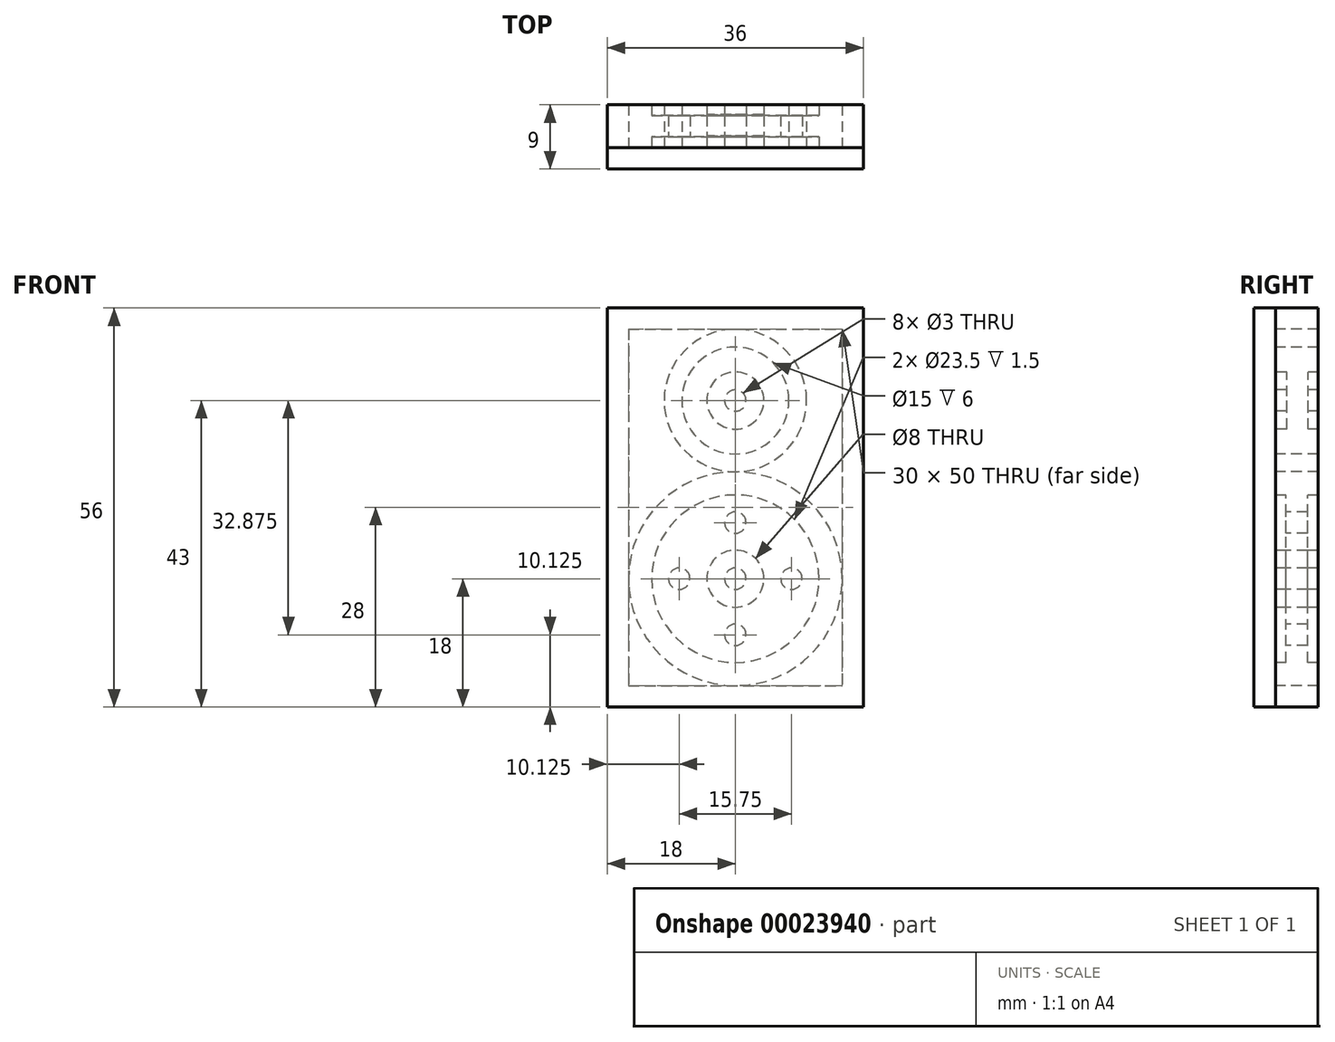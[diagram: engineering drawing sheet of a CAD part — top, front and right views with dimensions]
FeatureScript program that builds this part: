
annotation { "Feature Type Name" : "Feature", "Feature Type Description" : "" }
export const myFeature = defineFeature(function(context is Context, id is Id, definition is map)
    precondition{}
    {
        {
            var Q0;
            Q0=qCreatedBy(makeId("Right.planeOp"),FACE);
            var sketch = newSketch(context, id + "F0", { "sketchPlane" : qUnion([Q0])});
            skLineSegment(sketch, "E0.rect.bottom", {"start": v(-3, 1.5) * mm, "end": v(3, 1.5) * mm});
            skLineSegment(sketch, "E0.rect.top", {"start": v(-3, 4) * mm, "end": v(3, 4) * mm});
            skLineSegment(sketch, "E0.rect.left", {"start": v(-3, 4) * mm, "end": v(-3, 1.5) * mm});
            skLineSegment(sketch, "E0.rect.right", {"start": v(3, 4) * mm, "end": v(3, 1.5) * mm});
            skPoint(sketch, "E0.rect.middle", {"position": v(0, 2.75) * mm});
            skLineSegment(sketch, "E1.rect.bottom", {"start": v(1.5, 1.5) * mm, "end": v(-1.5, 1.5) * mm});
            skLineSegment(sketch, "E1.rect.top", {"start": v(1.5, 11.75) * mm, "end": v(-1.5, 11.75) * mm});
            skLineSegment(sketch, "E1.rect.left", {"start": v(1.5, 1.5) * mm, "end": v(1.5, 11.75) * mm});
            skLineSegment(sketch, "E1.rect.right", {"start": v(-1.5, 1.5) * mm, "end": v(-1.5, 11.75) * mm});
            skPoint(sketch, "E1.rect.middle", {"position": v(0, 6.62) * mm});
            skLineSegment(sketch, "E2.rect.bottom", {"start": v(-3, 15) * mm, "end": v(3, 15) * mm});
            skLineSegment(sketch, "E2.rect.left", {"start": v(-3, 15) * mm, "end": v(-3, 11.75) * mm});
            skLineSegment(sketch, "E2.rect.top", {"start": v(-3, 11.75) * mm, "end": v(3, 11.75) * mm});
            skLineSegment(sketch, "E2.rect.right", {"start": v(3, 15) * mm, "end": v(3, 11.75) * mm});
            skLineSegment(sketch, "E3", {"start": v(-14.88, 0) * mm, "end": v(15.69, 0) * mm, "construction": true});
            skLineSegment(sketch, "E4", {"start": v(1.5, 1.5) * mm, "end": v(3, 1.5) * mm});
            skLineSegment(sketch, "E5", {"start": v(-3, 1.5) * mm, "end": v(-1.5, 1.5) * mm});
            skLineSegment(sketch, "E6", {"start": v(-3, 4) * mm, "end": v(-3, 11.75) * mm, "construction": true});
            skLineSegment(sketch, "E7", {"start": v(3, 4) * mm, "end": v(3, 11.75) * mm, "construction": true});
            skPoint(sketch, "E8.rect.middle", {"position": v(0.12, 29.5) * mm});
            skLineSegment(sketch, "E9", {"start": v(-3, 29) * mm, "end": v(-3, 32.5) * mm, "construction": true});
            skLineSegment(sketch, "E10.rect.bottom", {"start": v(-3, 26.5) * mm, "end": v(3, 26.5) * mm});
            skLineSegment(sketch, "E10.rect.top", {"start": v(-3, 29) * mm, "end": v(3, 29) * mm});
            skLineSegment(sketch, "E10.rect.left", {"start": v(-3, 29) * mm, "end": v(-3, 26.5) * mm});
            skLineSegment(sketch, "E10.rect.right", {"start": v(3, 29) * mm, "end": v(3, 26.5) * mm});
            skPoint(sketch, "E10.rect.middle", {"position": v(0, 27.75) * mm});
            skLineSegment(sketch, "E8.rect.bottom", {"start": v(1.62, 26.5) * mm, "end": v(-1.38, 26.5) * mm});
            skLineSegment(sketch, "E8.rect.left", {"start": v(1.62, 26.5) * mm, "end": v(1.62, 32.5) * mm});
            skLineSegment(sketch, "E8.rect.right", {"start": v(-1.38, 26.5) * mm, "end": v(-1.38, 32.5) * mm});
            skLineSegment(sketch, "E11.rect.bottom", {"start": v(-3, 35) * mm, "end": v(3, 35) * mm});
            skLineSegment(sketch, "E11.rect.left", {"start": v(-3, 35) * mm, "end": v(-3, 32.5) * mm});
            skLineSegment(sketch, "E11.rect.top", {"start": v(-3, 32.5) * mm, "end": v(3, 32.5) * mm});
            skLineSegment(sketch, "E11.rect.right", {"start": v(3, 35) * mm, "end": v(3, 32.5) * mm});
            skLineSegment(sketch, "E12", {"start": v(3, 29) * mm, "end": v(3, 32.5) * mm, "construction": true});
            skLineSegment(sketch, "E13", {"start": v(1.62, 26.5) * mm, "end": v(3, 26.5) * mm});
            skLineSegment(sketch, "E14", {"start": v(-3, 26.5) * mm, "end": v(-1.38, 26.5) * mm});
            skLineSegment(sketch, "E8.rect.top", {"start": v(1.62, 32.5) * mm, "end": v(-1.38, 32.5) * mm});
            skLineSegment(sketch, "E15", {"start": v(-18.67, 25) * mm, "end": v(16.68, 25) * mm, "construction": true});
            skLineSegment(sketch, "E16", {"start": v(-3, 1.5) * mm, "end": v(-3, 38.38) * mm, "construction": true});
            skLineSegment(sketch, "E17", {"start": v(3, 1.5) * mm, "end": v(3, 82.02) * mm, "construction": true});
            skSolve(sketch);
        }
        {
            var Q0;
            Q0=makeQuery(id+"F0.imprint","IMPRINT",FACE,{"disambiguationData":[TD([[makeQuery(id+"F0.imprint","IMPRINT",EDGE,{"derivedFrom":sQuery(id+"F0.wireOp",EDGE,"E2.rect.bottom")}),-1.0]])]});
            var Q1;
            {var subQ1=sQuery(id+"F0.wireOp",EDGE,"E1.rect.right");var subQ5=sQuery(id+"F0.wireOp",EDGE,"E0.rect.top");var subQ6=makeQuery(id+"F0.imprint","INTERSECT",VERTEX,{"derivedFrom":[subQ5,subQ1]});Q1=makeQuery(id+"F0.imprint","IMPRINT",FACE,{"disambiguationData":[TD([[makeQuery(id+"F0.imprint","IMPRINT",EDGE,{"disambiguationData":[TD([[subQ6,-1.0]])],"derivedFrom":subQ5}),1.0]])]});}
            var Q2;
            {var subQ4=sQuery(id+"F0.wireOp",EDGE,"E1.rect.bottom");Q2=makeQuery(id+"F0.imprint","IMPRINT",FACE,{"disambiguationData":[TD([[makeQuery(id+"F0.imprint","IMPRINT",EDGE,{"derivedFrom":subQ4}),-1.0]])]});}
            var Q3;
            {var subQ5=sQuery(id+"F0.wireOp",EDGE,"E0.rect.left");Q3=makeQuery(id+"F0.imprint","IMPRINT",FACE,{"disambiguationData":[TD([[makeQuery(id+"F0.imprint","IMPRINT",EDGE,{"derivedFrom":subQ5}),1.0]])]});}
            var Q4;
            {var subQ5=sQuery(id+"F0.wireOp",EDGE,"E0.rect.right");Q4=makeQuery(id+"F0.imprint","IMPRINT",FACE,{"disambiguationData":[TD([[makeQuery(id+"F0.imprint","IMPRINT",EDGE,{"derivedFrom":subQ5}),-1.0]])]});}
            var Q5;
            Q5=sQuery(id+"F0.wireOp",EDGE,"E3");
            revolve(context, id + "F1", {"entities" : qUnion([Q0, Q1, Q2, Q3, Q4]), "axis" : qUnion([Q5]), "revolveType" : RevolveType.FULL});
        }
        {
            var Q0;
            Q0=makeQuery(id+"F1.opRevolve","SWEPT_FACE",FACE,{"disambiguationData":[OSD([sQuery(id+"F0.wireOp",EDGE,"E1.rect.right")])]});
            var sketch = newSketch(context, id + "F2", { "sketchPlane" : qUnion([Q0])});
            skCircle(sketch, "E18", {"center": v(0, 7.88) * mm, "radius": 1.5 * mm});
            skLineSegment(sketch, "E19", {"start": v(0, 4) * mm, "end": v(0, 6.38) * mm, "construction": true});
            skLineSegment(sketch, "E20", {"start": v(0, 9.38) * mm, "end": v(0, 11.75) * mm, "construction": true});
            skCircle(sketch, "E21.1.0", {"center": v(-7.88, 0) * mm, "radius": 1.5 * mm});
            skCircle(sketch, "E21.2.0", {"center": v(0, -7.88) * mm, "radius": 1.5 * mm});
            skCircle(sketch, "E21.3.0", {"center": v(7.88, 0) * mm, "radius": 1.5 * mm});
            skPoint(sketch, "E21.center", {"position": v(0, 0) * mm});
            skSolve(sketch);
        }
        {
            var Q0;
            Q0=makeQuery(id+"F2.imprint","IMPRINT",FACE,{"disambiguationData":[TD([[makeQuery(id+"F2.imprint","IMPRINT",EDGE,{"derivedFrom":sQuery(id+"F2.wireOp",EDGE,"E18")}),1.0]])]});
            var Q1;
            Q1=makeQuery(id+"F2.imprint","IMPRINT",FACE,{"disambiguationData":[TD([[makeQuery(id+"F2.imprint","IMPRINT",EDGE,{"derivedFrom":sQuery(id+"F2.wireOp",EDGE,"E21.3.0")}),1.0]])]});
            var Q2;
            Q2=makeQuery(id+"F2.imprint","IMPRINT",FACE,{"disambiguationData":[TD([[makeQuery(id+"F2.imprint","IMPRINT",EDGE,{"derivedFrom":sQuery(id+"F2.wireOp",EDGE,"E21.1.0")}),1.0]])]});
            var Q3;
            Q3=makeQuery(id+"F2.imprint","IMPRINT",FACE,{"disambiguationData":[TD([[makeQuery(id+"F2.imprint","IMPRINT",EDGE,{"derivedFrom":sQuery(id+"F2.wireOp",EDGE,"E21.2.0")}),1.0]])]});
            extrude(context, id + "F3", {"entities" : qUnion([Q0, Q1, Q2, Q3]), "operationType" : NewBodyOperationType.REMOVE, "oppositeDirection" : true, "depth" : 3 * mm});
        }
        {
            var Q0;
            {var subQ3=sQuery(id+"F0.wireOp",EDGE,"E8.rect.bottom");Q0=makeQuery(id+"F0.imprint","IMPRINT",FACE,{"disambiguationData":[TD([[makeQuery(id+"F0.imprint","IMPRINT",EDGE,{"derivedFrom":subQ3}),-1.0]])]});}
            var Q1;
            {var subQ0=sQuery(id+"F0.wireOp",EDGE,"E8.rect.top");Q1=makeQuery(id+"F0.imprint","IMPRINT",FACE,{"disambiguationData":[TD([[makeQuery(id+"F0.imprint","IMPRINT",EDGE,{"derivedFrom":subQ0}),1.0]])]});}
            var Q2;
            Q2=makeQuery(id+"F0.imprint","IMPRINT",FACE,{"disambiguationData":[TD([[makeQuery(id+"F0.imprint","IMPRINT",EDGE,{"derivedFrom":sQuery(id+"F0.wireOp",EDGE,"E11.rect.bottom")}),-1.0]])]});
            var Q3;
            {var subQ4=sQuery(id+"F0.wireOp",EDGE,"E10.rect.right");Q3=makeQuery(id+"F0.imprint","IMPRINT",FACE,{"disambiguationData":[TD([[makeQuery(id+"F0.imprint","IMPRINT",EDGE,{"derivedFrom":subQ4}),-1.0]])]});}
            var Q4;
            {var subQ4=sQuery(id+"F0.wireOp",EDGE,"E10.rect.left");Q4=makeQuery(id+"F0.imprint","IMPRINT",FACE,{"disambiguationData":[TD([[makeQuery(id+"F0.imprint","IMPRINT",EDGE,{"derivedFrom":subQ4}),1.0]])]});}
            var Q5;
            Q5=sQuery(id+"F0.wireOp",EDGE,"E15");
            revolve(context, id + "F4", {"entities" : qUnion([Q0, Q1, Q2, Q3, Q4]), "axis" : qUnion([Q5]), "revolveType" : RevolveType.FULL});
        }
        {
            var Q0;
            Q0=makeQuery(id+"F4.opRevolve","SWEPT_FACE",FACE,{"disambiguationData":[OSD([sQuery(id+"F0.wireOp",EDGE,"E8.rect.right")])]});
            var sketch = newSketch(context, id + "F5", { "sketchPlane" : qUnion([Q0])});
            skCircle(sketch, "E22", {"center": v(0, 30.75) * mm, "radius": 1.5 * mm});
            skLineSegment(sketch, "E23", {"start": v(0, 32.25) * mm, "end": v(0, 32.5) * mm});
            skLineSegment(sketch, "E24", {"start": v(0, 29.25) * mm, "end": v(0, 29) * mm});
            skCircle(sketch, "E25.1.0", {"center": v(-5.75, 25) * mm, "radius": 1.5 * mm});
            skCircle(sketch, "E25.2.0", {"center": v(0, 19.25) * mm, "radius": 1.5 * mm});
            skCircle(sketch, "E25.3.0", {"center": v(5.75, 25) * mm, "radius": 1.5 * mm});
            skPoint(sketch, "E25.center", {"position": v(0, 25) * mm});
            skSolve(sketch);
        }
        {
            var Q0;
            Q0=makeQuery(id+"F5.imprint","IMPRINT",FACE,{"disambiguationData":[TD([[makeQuery(id+"F5.imprint","IMPRINT",EDGE,{"derivedFrom":sQuery(id+"F5.wireOp",EDGE,"E25.1.0")}),1.0]])]});
            var Q1;
            {var subQ0=sQuery(id+"F5.wireOp",EDGE,"E22");var subQ2=makeQuery(id+"F5.imprint","IMPRINT",VERTEX,{"disambiguationData":[OD(0.0)],"derivedFrom":subQ0});Q1=makeQuery(id+"F5.imprint","IMPRINT",FACE,{"disambiguationData":[TD([[makeQuery(id+"F5.imprint","IMPRINT",EDGE,{"disambiguationData":[TD([[subQ2,-1.0]])],"derivedFrom":subQ0}),1.0]])]});}
            var Q2;
            Q2=makeQuery(id+"F5.imprint","IMPRINT",FACE,{"disambiguationData":[TD([[makeQuery(id+"F5.imprint","IMPRINT",EDGE,{"derivedFrom":sQuery(id+"F5.wireOp",EDGE,"E25.3.0")}),1.0]])]});
            var Q3;
            Q3=makeQuery(id+"F5.imprint","IMPRINT",FACE,{"disambiguationData":[TD([[makeQuery(id+"F5.imprint","IMPRINT",EDGE,{"derivedFrom":sQuery(id+"F5.wireOp",EDGE,"E25.2.0")}),1.0]])]});
            extrude(context, id + "F6", {"entities" : qUnion([Q0, Q1, Q2, Q3]), "operationType" : NewBodyOperationType.REMOVE, "oppositeDirection" : true, "depth" : 3 * mm});
        }
        {
            var Q0;
            Q0=makeQuery(id+"F4.opRevolve","SWEPT_FACE",FACE,{"disambiguationData":[OSD([sQuery(id+"F0.wireOp",EDGE,"E11.rect.left")])]});
            var sketch = newSketch(context, id + "F7", { "sketchPlane" : qUnion([Q0])});
            skLineSegment(sketch, "E26.bottom", {"start": v(-15, 35) * mm, "end": v(15, 35) * mm});
            skLineSegment(sketch, "E26.top", {"start": v(-15, -15) * mm, "end": v(15, -15) * mm});
            skLineSegment(sketch, "E26.left", {"start": v(-15, 35) * mm, "end": v(-15, -15) * mm});
            skLineSegment(sketch, "E26.right", {"start": v(15, 35) * mm, "end": v(15, -15) * mm});
            skLineSegment(sketch, "E27.0", {"start": v(-18, 38) * mm, "end": v(18, 38) * mm});
            skLineSegment(sketch, "E27.1", {"start": v(-18, 38) * mm, "end": v(-18, -18) * mm});
            skLineSegment(sketch, "E27.2", {"start": v(-18, -18) * mm, "end": v(18, -18) * mm});
            skLineSegment(sketch, "E27.3", {"start": v(18, 38) * mm, "end": v(18, -18) * mm});
            skSolve(sketch);
        }
        {
            var Q0;
            Q0=makeQuery(id+"F7.imprint","IMPRINT",FACE,{"disambiguationData":[TD([[makeQuery(id+"F7.imprint","IMPRINT",EDGE,{"derivedFrom":sQuery(id+"F7.wireOp",EDGE,"E26.top")}),-1.0]])]});
            extrude(context, id + "F8", {"entities" : qUnion([Q0]), "oppositeDirection" : true, "depth" : 6 * mm});
        }
        {
            var Q0;
            Q0=makeQuery(id+"F1.opRevolve","SWEPT_FACE",FACE,{"disambiguationData":[OSD([sQuery(id+"F0.wireOp",EDGE,"E2.rect.left")])]});
            var sketch = newSketch(context, id + "F9", { "sketchPlane" : qUnion([Q0])});
            skLineSegment(sketch, "E28.bottom", {"start": v(-18, 38) * mm, "end": v(18, 38) * mm});
            skLineSegment(sketch, "E28.top", {"start": v(-18, -18) * mm, "end": v(18, -18) * mm});
            skLineSegment(sketch, "E28.left", {"start": v(-18, 38) * mm, "end": v(-18, -18) * mm});
            skLineSegment(sketch, "E28.right", {"start": v(18, 38) * mm, "end": v(18, -18) * mm});
            skSolve(sketch);
        }
        {
            var Q0;
            Q0=makeQuery(id+"F9.imprint","IMPRINT",FACE,{"disambiguationData":[TD([[makeQuery(id+"F9.imprint","IMPRINT",EDGE,{"derivedFrom":sQuery(id+"F9.wireOp",EDGE,"E28.bottom")}),-1.0]])]});
            var Q1;
            {var subQ0=sQuery(id+"F0.wireOp",EDGE,"E2.rect.left");Q1=makeQuery(id+"F9.imprint","IMPRINT",FACE,{"disambiguationData":[TD([[makeQuery(id+"F9.imprint","IMPRINT",EDGE,{"derivedFrom":makeQuery(id+"F1.opRevolve","SWEPT_EDGE",EDGE,{"disambiguationData":[OSD([sQuery(id+"F0.wireOp",EDGE,"E2.rect.bottom"),subQ0])]})}),1.0]])]});}
            var Q2;
            Q2=makeQuery(id+"F9.imprint","IMPRINT",FACE,{"disambiguationData":[TD([[makeQuery(id+"F9.imprint","IMPRINT",EDGE,{"derivedFrom":makeQuery(id+"F1.opRevolve","SWEPT_EDGE",EDGE,{"disambiguationData":[OSD([sQuery(id+"F0.wireOp",EDGE,"E2.rect.left"),sQuery(id+"F0.wireOp",EDGE,"E2.rect.top")])]})}),1.0]])]});
            extrude(context, id + "F10", {"entities" : qUnion([Q0, Q1, Q2]), "depth" : 3 * mm});
        }
    });
